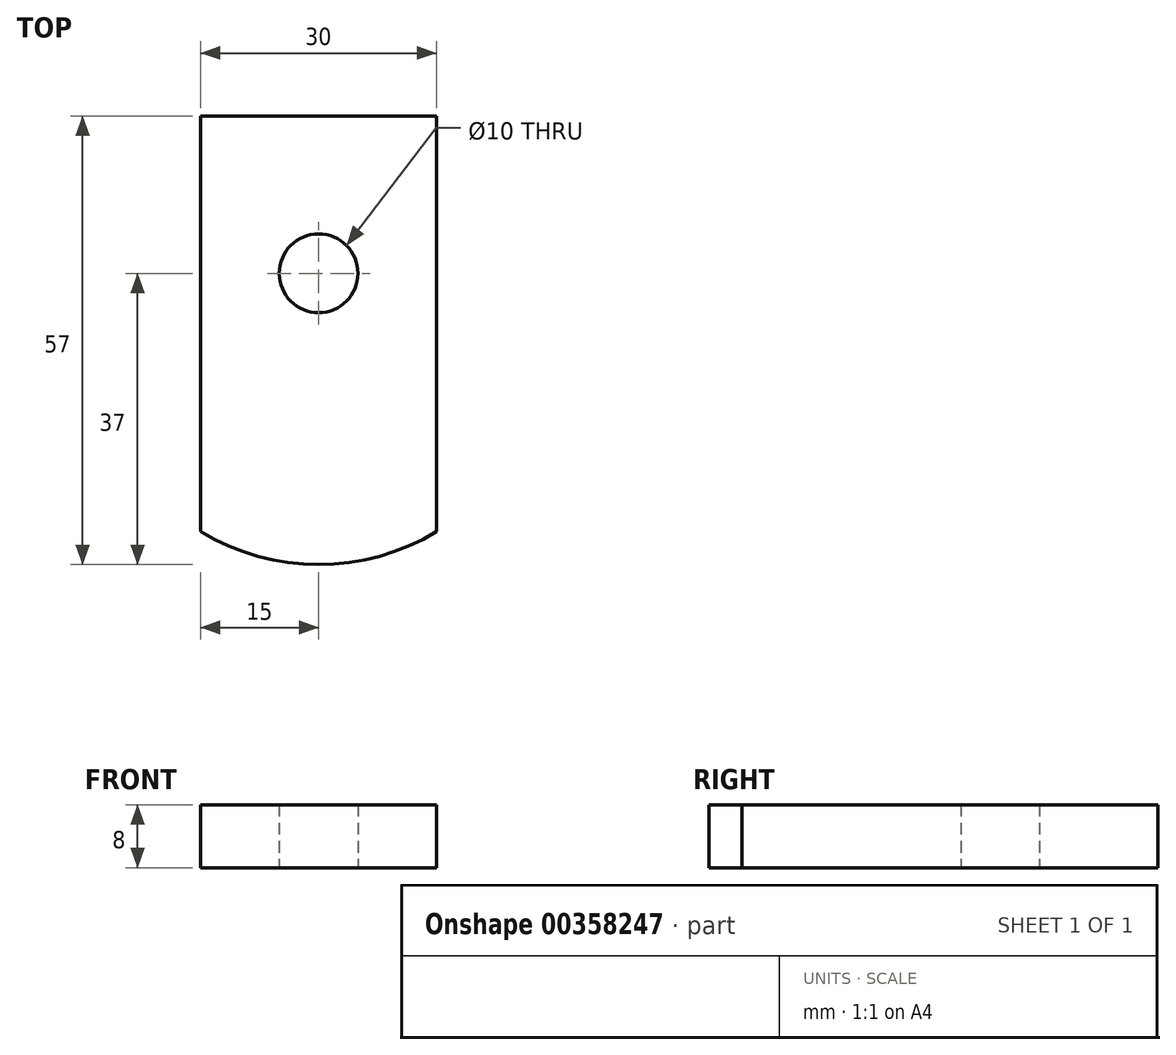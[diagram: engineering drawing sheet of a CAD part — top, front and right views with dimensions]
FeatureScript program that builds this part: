
annotation { "Feature Type Name" : "Feature", "Feature Type Description" : "" }
export const myFeature = defineFeature(function(context is Context, id is Id, definition is map)
    precondition{}
    {
        {
            var Q0;
            Q0=qCreatedBy(makeId("Top.planeOp"),FACE);
            var sketch = newSketch(context, id + "F0", { "sketchPlane" : qUnion([Q0])});
            skCircle(sketch, "E0", {"center": v(0, 0) * mm, "radius": 5 * mm});
            skLineSegment(sketch, "E1.bottom", {"start": v(-15, 20) * mm, "end": v(15, 20) * mm});
            skLineSegment(sketch, "E1.left", {"start": v(-15, 20) * mm, "end": v(-15, -32.82) * mm});
            skLineSegment(sketch, "E1.right", {"start": v(15, 20) * mm, "end": v(15, -32.82) * mm});
            skArc(sketch, "E2", {"start": v(-15, -32.82) * mm, "mid": v(0, -37) * mm, "end": v(15, -32.82) * mm});
            skSolve(sketch);
        }
        {
            var Q0;
            Q0=makeQuery(id+"F0.imprint","IMPRINT",FACE,{"disambiguationData":[TD([[makeQuery(id+"F0.imprint","IMPRINT",EDGE,{"derivedFrom":sQuery(id+"F0.wireOp",EDGE,"E0")}),-1.0]])]});
            extrude(context, id + "F1", {"entities" : qUnion([Q0]), "depth" : 8 * mm});
        }
    });
